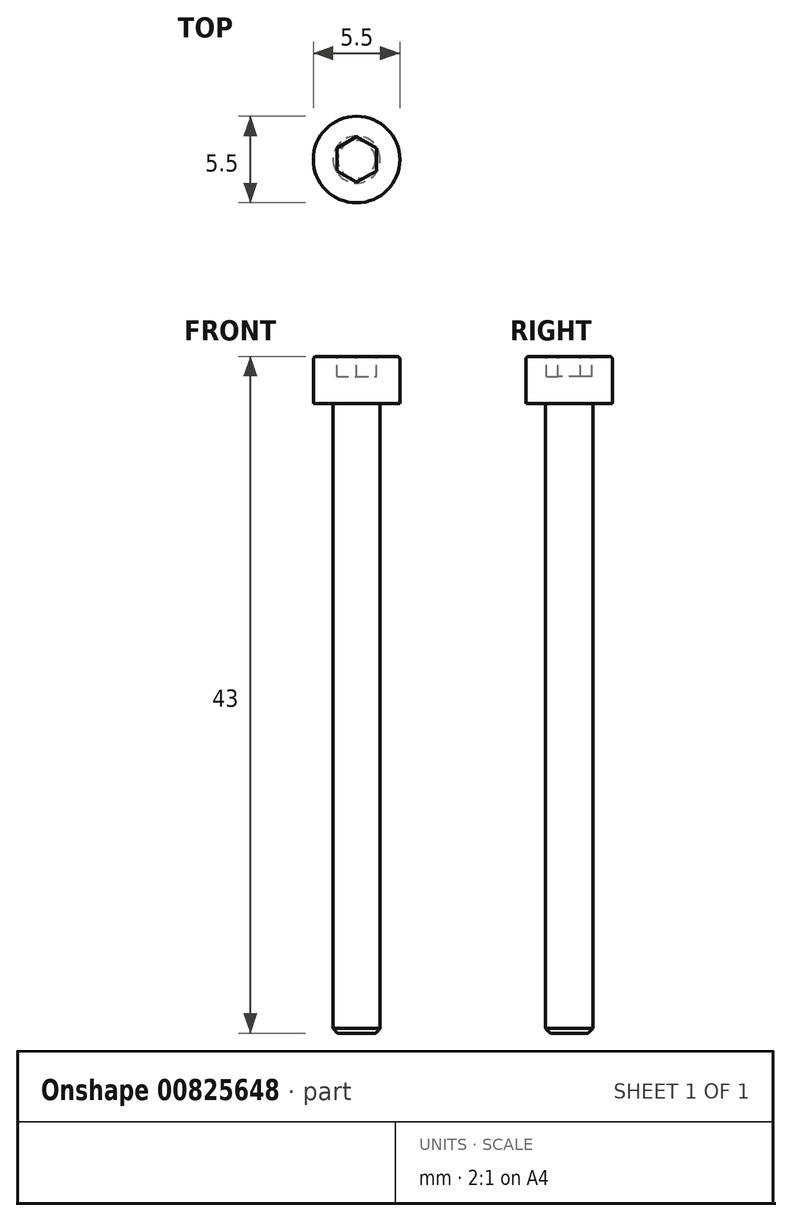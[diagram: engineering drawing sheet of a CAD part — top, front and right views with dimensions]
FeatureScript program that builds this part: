
annotation { "Feature Type Name" : "Feature", "Feature Type Description" : "" }
export const myFeature = defineFeature(function(context is Context, id is Id, definition is map)
    precondition{}
    {
        {
            assignVariable(context, id + "F0", {"name" : "Head_t", "anyValue" : 1.3});
        }
        {
            var Q0;
            Q0=qCreatedBy(makeId("Front.planeOp"),FACE);
            var sketch = newSketch(context, id + "F1", { "sketchPlane" : qUnion([Q0])});
            skLineSegment(sketch, "E0", {"start": v(0, 3) * mm, "end": v(2.55, 3) * mm});
            skLineSegment(sketch, "E1", {"start": v(2.75, 2.8) * mm, "end": v(2.75, 0) * mm});
            skLineSegment(sketch, "E2", {"start": v(2.75, 0) * mm, "end": v(0, 0) * mm});
            skLineSegment(sketch, "E3", {"start": v(0, 0) * mm, "end": v(0, 3) * mm});
            skPoint(sketch, "E4.orphan", {"position": v(0, -40) * mm});
            skPoint(sketch, "E5.visualSharp", {"position": v(2.75, 3) * mm});
            skArc(sketch, "E5.filletArc", {"start": v(2.75, 2.8) * mm, "mid": v(2.7, 2.94) * mm, "end": v(2.55, 3) * mm});
            skSolve(sketch);
        }
        {
            var Q0;
            Q0=makeQuery(id+"F1.imprint","IMPRINT",FACE,{"disambiguationData":[TD([[makeQuery(id+"F1.imprint","IMPRINT",EDGE,{"derivedFrom":sQuery(id+"F1.wireOp",EDGE,"E0")}),-1.0]])]});
            var Q1;
            Q1=sQuery(id+"F1.wireOp",EDGE,"E3");
            revolve(context, id + "F2", {"entities" : qUnion([Q0]), "axis" : qUnion([Q1]), "revolveType" : RevolveType.FULL});
        }
        {
            var Q0;
            Q0=makeQuery(id+"F2.opRevolve","SWEPT_FACE",FACE,{"disambiguationData":[OSD([sQuery(id+"F1.wireOp",EDGE,"E0")])]});
            var sketch = newSketch(context, id + "F3", { "sketchPlane" : qUnion([Q0])});
            skCircle(sketch, "E6.cCircle", {"center": v(0, 0) * mm, "radius": 1.25 * mm, "construction": true});
            skLineSegment(sketch, "E6.0", {"start": v(1.25, 0.72) * mm, "end": v(1.25, -0.72) * mm});
            skLineSegment(sketch, "E6.1", {"start": v(1.25, -0.72) * mm, "end": v(0, -1.44) * mm});
            skLineSegment(sketch, "E6.2", {"start": v(0, -1.44) * mm, "end": v(-1.25, -0.72) * mm});
            skLineSegment(sketch, "E6.3", {"start": v(-1.25, -0.72) * mm, "end": v(-1.25, 0.72) * mm});
            skLineSegment(sketch, "E6.4", {"start": v(-1.25, 0.72) * mm, "end": v(0, 1.44) * mm});
            skLineSegment(sketch, "E6.5", {"start": v(0, 1.44) * mm, "end": v(1.25, 0.72) * mm});
            skPoint(sketch, "E6.0.midPoint", {"position": v(1.25, 0) * mm});
            skSolve(sketch);
        }
        {
            var Q0;
            Q0=qSketchRegion(id+"F3",true);
            extrude(context, id + "F4", {"entities" : qUnion([Q0]), "operationType" : NewBodyOperationType.REMOVE, "oppositeDirection" : true, "depth" : (getVariable(context, 'Head_t')) * mm});
        }
        {
            var Q0;
            Q0=makeQuery(id+"F2.opRevolve","SWEPT_BODY",BODY,{"disambiguationData":[OSD([sQuery(id+"F1.wireOp",EDGE,"E0"),sQuery(id+"F1.wireOp",EDGE,"E1"),sQuery(id+"F1.wireOp",EDGE,"E2"),sQuery(id+"F1.wireOp",EDGE,"E3")])]});
            transform(context, id + "F5", {"entities" : qUnion([Q0]), "transformType" : TransformType.TRANSLATION_3D, "dx" : 0 * mm, "dy" : 0 * mm, "dz" : 0 * mm, "makeCopy" : true});
        }
        {
            var Q0;
            Q0=qCreatedBy(makeId("Front.planeOp"),FACE);
            var sketch = newSketch(context, id + "F6", { "sketchPlane" : qUnion([Q0])});
            skLineSegment(sketch, "E7.bottom", {"start": v(0, 0) * mm, "end": v(1.5, 0) * mm});
            skLineSegment(sketch, "E7.top", {"start": v(0, -8) * mm, "end": v(1.2, -8) * mm});
            skLineSegment(sketch, "E7.left", {"start": v(0, 0) * mm, "end": v(0, -8) * mm});
            skLineSegment(sketch, "E7.right", {"start": v(1.5, 0) * mm, "end": v(1.5, -7.7) * mm});
            skLineSegment(sketch, "E8", {"start": v(1.2, -8) * mm, "end": v(1.5, -7.7) * mm});
            skSolve(sketch);
        }
        {
            var Q0;
            Q0=qSketchRegion(id+"F6",true);
            var Q1;
            Q1=sQuery(id+"F6.wireOp",EDGE,"E7.left");
            revolve(context, id + "F7", {"operationType" : NewBodyOperationType.ADD, "entities" : qUnion([Q0]), "axis" : qUnion([Q1]), "revolveType" : RevolveType.FULL});
        }
        {
            var Q0;
            Q0=makeQuery(id+"F2.opRevolve","SWEPT_BODY",BODY,{"disambiguationData":[OSD([sQuery(id+"F1.wireOp",EDGE,"E0"),sQuery(id+"F1.wireOp",EDGE,"E1"),sQuery(id+"F1.wireOp",EDGE,"E2"),sQuery(id+"F1.wireOp",EDGE,"E3")])]});
            transform(context, id + "F8", {"entities" : qUnion([Q0]), "transformType" : TransformType.TRANSLATION_3D, "dx" : 0 * mm, "dy" : 0 * mm, "dz" : 0 * mm, "makeCopy" : true});
        }
        {
            var Q0;
            Q0=qCreatedBy(makeId("Front.planeOp"),FACE);
            var sketch = newSketch(context, id + "F9", { "sketchPlane" : qUnion([Q0])});
            skLineSegment(sketch, "E9.bottom", {"start": v(0, 0) * mm, "end": v(1.5, 0) * mm});
            skLineSegment(sketch, "E9.top", {"start": v(0, -10) * mm, "end": v(1.2, -10) * mm});
            skLineSegment(sketch, "E9.left", {"start": v(0, 0) * mm, "end": v(0, -10) * mm});
            skLineSegment(sketch, "E9.right", {"start": v(1.5, 0) * mm, "end": v(1.5, -9.7) * mm});
            skLineSegment(sketch, "E10", {"start": v(1.2, -10) * mm, "end": v(1.5, -9.7) * mm});
            skSolve(sketch);
        }
        {
            var Q0;
            Q0=qSketchRegion(id+"F9",true);
            var Q1;
            Q1=sQuery(id+"F9.wireOp",EDGE,"E9.left");
            revolve(context, id + "F10", {"operationType" : NewBodyOperationType.ADD, "entities" : qUnion([Q0]), "axis" : qUnion([Q1]), "revolveType" : RevolveType.FULL});
        }
        {
            var Q0;
            Q0=makeQuery(id+"F2.opRevolve","SWEPT_BODY",BODY,{"disambiguationData":[OSD([sQuery(id+"F1.wireOp",EDGE,"E0"),sQuery(id+"F1.wireOp",EDGE,"E1"),sQuery(id+"F1.wireOp",EDGE,"E2"),sQuery(id+"F1.wireOp",EDGE,"E3"),sQuery(id+"F1.wireOp",EDGE,"E5.filletArc")])]});
            transform(context, id + "F11", {"entities" : qUnion([Q0]), "transformType" : TransformType.TRANSLATION_3D, "dx" : 0 * mm, "dy" : 0 * mm, "dz" : 0 * mm, "makeCopy" : true});
        }
        {
            var Q0;
            Q0=qCreatedBy(makeId("Front.planeOp"),FACE);
            var sketch = newSketch(context, id + "F12", { "sketchPlane" : qUnion([Q0])});
            skLineSegment(sketch, "E11.bottom", {"start": v(0, 0) * mm, "end": v(1.5, 0) * mm});
            skLineSegment(sketch, "E11.top", {"start": v(0, -30) * mm, "end": v(1.2, -30) * mm});
            skLineSegment(sketch, "E11.left", {"start": v(0, 0) * mm, "end": v(0, -30) * mm});
            skLineSegment(sketch, "E11.right", {"start": v(1.5, 0) * mm, "end": v(1.5, -29.7) * mm});
            skLineSegment(sketch, "E12", {"start": v(1.2, -30) * mm, "end": v(1.5, -29.7) * mm});
            skSolve(sketch);
        }
        {
            var Q0;
            Q0=qSketchRegion(id+"F12",true);
            var Q1;
            Q1=sQuery(id+"F12.wireOp",EDGE,"E11.left");
            revolve(context, id + "F13", {"operationType" : NewBodyOperationType.ADD, "entities" : qUnion([Q0]), "axis" : qUnion([Q1]), "revolveType" : RevolveType.FULL});
        }
        {
            var Q0;
            Q0=makeQuery(id+"F2.opRevolve","SWEPT_BODY",BODY,{"disambiguationData":[OSD([sQuery(id+"F1.wireOp",EDGE,"E0"),sQuery(id+"F1.wireOp",EDGE,"E1"),sQuery(id+"F1.wireOp",EDGE,"E2"),sQuery(id+"F1.wireOp",EDGE,"E3"),sQuery(id+"F1.wireOp",EDGE,"E5.filletArc")])]});
            transform(context, id + "F14", {"entities" : qUnion([Q0]), "transformType" : TransformType.TRANSLATION_3D, "dx" : 0 * mm, "dy" : 0 * mm, "dz" : 0 * mm, "makeCopy" : true});
        }
        {
            var Q0;
            Q0=qCreatedBy(makeId("Front.planeOp"),FACE);
            var sketch = newSketch(context, id + "F15", { "sketchPlane" : qUnion([Q0])});
            skLineSegment(sketch, "E13.bottom", {"start": v(0, 0) * mm, "end": v(1.5, 0) * mm});
            skLineSegment(sketch, "E13.top", {"start": v(0, -40) * mm, "end": v(1.2, -40) * mm});
            skLineSegment(sketch, "E13.left", {"start": v(0, 0) * mm, "end": v(0, -40) * mm});
            skLineSegment(sketch, "E13.right", {"start": v(1.5, 0) * mm, "end": v(1.5, -39.7) * mm});
            skLineSegment(sketch, "E14", {"start": v(1.2, -40) * mm, "end": v(1.5, -39.7) * mm});
            skLineSegment(sketch, "E15", {"start": v(1.48, -22) * mm, "end": v(3, -22) * mm});
            skLineSegment(sketch, "E16", {"start": v(3, -22) * mm, "end": v(3, -22.88) * mm});
            skLineSegment(sketch, "E17", {"start": v(3, -22.88) * mm, "end": v(1.48, -22) * mm});
            skSolve(sketch);
        }
        {
            var Q0;
            {var subQ1=sQuery(id+"F15.wireOp",EDGE,"E13.bottom");Q0=makeQuery(id+"F15.imprint","IMPRINT",FACE,{"disambiguationData":[TD([[makeQuery(id+"F15.imprint","IMPRINT",EDGE,{"derivedFrom":subQ1}),-1.0]])]});}
            var Q1;
            Q1=sQuery(id+"F15.wireOp",EDGE,"E13.left");
            revolve(context, id + "F16", {"operationType" : NewBodyOperationType.ADD, "entities" : qUnion([Q0]), "axis" : qUnion([Q1]), "revolveType" : RevolveType.FULL});
        }
        {
            var Q0;
            Q0=makeQuery(id+"F2.opRevolve","SWEPT_BODY",BODY,{"disambiguationData":[OSD([sQuery(id+"F1.wireOp",EDGE,"E0"),sQuery(id+"F1.wireOp",EDGE,"E1"),sQuery(id+"F1.wireOp",EDGE,"E2"),sQuery(id+"F1.wireOp",EDGE,"E3"),sQuery(id+"F1.wireOp",EDGE,"E5.filletArc")])]});
            transform(context, id + "F17", {"entities" : qUnion([Q0]), "transformType" : TransformType.TRANSLATION_3D, "dx" : 0 * mm, "dy" : 0 * mm, "dz" : 0 * mm, "makeCopy" : true});
        }
        {
            var Q0;
            Q0=qCreatedBy(makeId("Front.planeOp"),FACE);
            var sketch = newSketch(context, id + "F18", { "sketchPlane" : qUnion([Q0])});
            skLineSegment(sketch, "E18.bottom", {"start": v(0, 0) * mm, "end": v(1.5, 0) * mm});
            skLineSegment(sketch, "E18.top", {"start": v(0, -6) * mm, "end": v(1.2, -6) * mm});
            skLineSegment(sketch, "E18.left", {"start": v(0, 0) * mm, "end": v(0, -6) * mm});
            skLineSegment(sketch, "E18.right", {"start": v(1.5, 0) * mm, "end": v(1.5, -5.7) * mm});
            skLineSegment(sketch, "E19", {"start": v(1.2, -6) * mm, "end": v(1.5, -5.7) * mm});
            skSolve(sketch);
        }
        {
            var Q0;
            Q0=qSketchRegion(id+"F18",true);
            var Q1;
            Q1=sQuery(id+"F18.wireOp",EDGE,"E18.left");
            revolve(context, id + "F19", {"operationType" : NewBodyOperationType.ADD, "entities" : qUnion([Q0]), "axis" : qUnion([Q1]), "revolveType" : RevolveType.FULL});
        }
        {
            var Q0;
            Q0=makeQuery(id+"F2.opRevolve","SWEPT_BODY",BODY,{"disambiguationData":[OSD([sQuery(id+"F1.wireOp",EDGE,"E0"),sQuery(id+"F1.wireOp",EDGE,"E1"),sQuery(id+"F1.wireOp",EDGE,"E2"),sQuery(id+"F1.wireOp",EDGE,"E3"),sQuery(id+"F1.wireOp",EDGE,"E5.filletArc")])]});
            transform(context, id + "F20", {"entities" : qUnion([Q0]), "transformType" : TransformType.TRANSLATION_3D, "dx" : 0 * mm, "dy" : 0 * mm, "dz" : 0 * mm, "makeCopy" : true});
        }
        {
            var Q0;
            Q0=qCreatedBy(makeId("Front.planeOp"),FACE);
            var sketch = newSketch(context, id + "F21", { "sketchPlane" : qUnion([Q0])});
            skLineSegment(sketch, "E20", {"start": v(0, 0) * mm, "end": v(1.5, 0) * mm});
            skLineSegment(sketch, "E21", {"start": v(1.5, 0) * mm, "end": v(1.5, -15.7) * mm});
            skLineSegment(sketch, "E22", {"start": v(1.5, -15.7) * mm, "end": v(1.2, -16) * mm});
            skLineSegment(sketch, "E23", {"start": v(1.2, -16) * mm, "end": v(0, -16) * mm});
            skLineSegment(sketch, "E24", {"start": v(0, -16) * mm, "end": v(0, 0) * mm});
            skSolve(sketch);
        }
        {
            var Q0;
            Q0 = qSketchRegion(id + "F21", true);
            var Q1;
            Q1=sQuery(id+"F21.wireOp",EDGE,"E24");
            revolve(context, id + "F22", {"operationType" : NewBodyOperationType.ADD, "surfaceOperationType" : NewSurfaceOperationType.NEW, "entities" : qUnion([Q0]), "axis" : qUnion([Q1]), "revolveType" : RevolveType.FULL});
        }
        {
            var Q0;
            Q0=makeQuery(id+"F2.opRevolve","SWEPT_BODY",BODY,{"disambiguationData":[OSD([sQuery(id+"F1.wireOp",EDGE,"E0"),sQuery(id+"F1.wireOp",EDGE,"E1"),sQuery(id+"F1.wireOp",EDGE,"E2"),sQuery(id+"F1.wireOp",EDGE,"E3"),sQuery(id+"F1.wireOp",EDGE,"E5.filletArc")])]});
            transform(context, id + "F23", {"entities" : qUnion([Q0]), "transformType" : TransformType.TRANSLATION_3D, "dx" : 0 * mm, "dy" : 0 * mm, "dz" : 0 * mm, "makeCopy" : true});
        }
        {
            var Q0;
            Q0=qCreatedBy(makeId("Front.planeOp"),FACE);
            var sketch = newSketch(context, id + "F24", { "sketchPlane" : qUnion([Q0])});
            skLineSegment(sketch, "E25", {"start": v(0, 0) * mm, "end": v(1.5, 0) * mm});
            skLineSegment(sketch, "E26", {"start": v(1.5, 0) * mm, "end": v(1.5, -11.7) * mm});
            skLineSegment(sketch, "E27", {"start": v(1.5, -11.7) * mm, "end": v(1.2, -12) * mm});
            skLineSegment(sketch, "E28", {"start": v(1.2, -12) * mm, "end": v(0, -12) * mm});
            skLineSegment(sketch, "E29", {"start": v(0, -12) * mm, "end": v(0, 0) * mm});
            skSolve(sketch);
        }
        {
            var Q0;
            Q0 = qSketchRegion(id + "F24", true);
            var Q1;
            Q1=sQuery(id+"F24.wireOp",EDGE,"E29");
            revolve(context, id + "F25", {"operationType" : NewBodyOperationType.ADD, "surfaceOperationType" : NewSurfaceOperationType.NEW, "entities" : qUnion([Q0]), "axis" : qUnion([Q1]), "revolveType" : RevolveType.FULL});
        }
        {
            var Q0;
            Q0=makeQuery(id+"F2.opRevolve","SWEPT_BODY",BODY,{"disambiguationData":[OSD([sQuery(id+"F1.wireOp",EDGE,"E0"),sQuery(id+"F1.wireOp",EDGE,"E1"),sQuery(id+"F1.wireOp",EDGE,"E2"),sQuery(id+"F1.wireOp",EDGE,"E3"),sQuery(id+"F1.wireOp",EDGE,"E5.filletArc")])]});
            transform(context, id + "F26", {"entities" : qUnion([Q0]), "transformType" : TransformType.TRANSLATION_3D, "dx" : 0 * mm, "dy" : 0 * mm, "dz" : 0 * mm, "makeCopy" : true});
        }
        {
            var Q0;
            Q0=qCreatedBy(makeId("Front.planeOp"),FACE);
            var sketch = newSketch(context, id + "F27", { "sketchPlane" : qUnion([Q0])});
            skLineSegment(sketch, "E30", {"start": v(0, 0) * mm, "end": v(1.5, 0) * mm});
            skLineSegment(sketch, "E31", {"start": v(1.5, 0) * mm, "end": v(1.5, -17.7) * mm});
            skLineSegment(sketch, "E32", {"start": v(1.5, -17.7) * mm, "end": v(1.2, -18) * mm});
            skLineSegment(sketch, "E33", {"start": v(1.2, -18) * mm, "end": v(0, -18) * mm});
            skLineSegment(sketch, "E34", {"start": v(0, -18) * mm, "end": v(0, 0) * mm});
            skSolve(sketch);
        }
        {
            var Q0;
            Q0 = qSketchRegion(id + "F27", true);
            var Q1;
            Q1=sQuery(id+"F27.wireOp",EDGE,"E34");
            revolve(context, id + "F28", {"operationType" : NewBodyOperationType.ADD, "surfaceOperationType" : NewSurfaceOperationType.NEW, "entities" : qUnion([Q0]), "axis" : qUnion([Q1]), "revolveType" : RevolveType.FULL});
        }
    });
